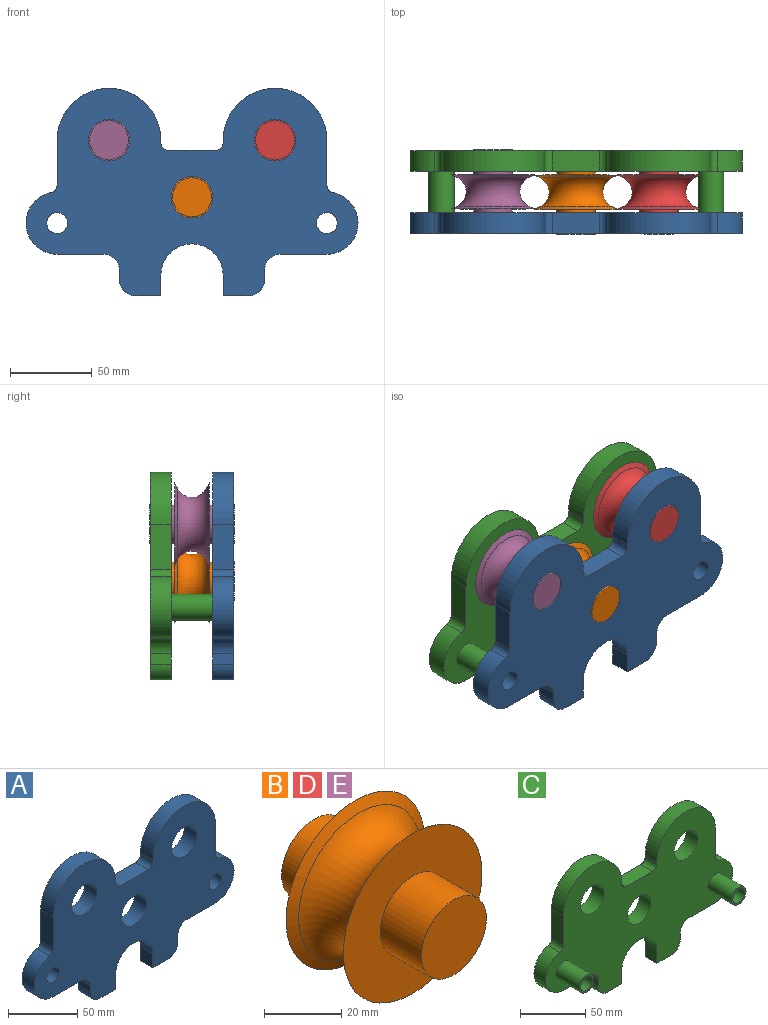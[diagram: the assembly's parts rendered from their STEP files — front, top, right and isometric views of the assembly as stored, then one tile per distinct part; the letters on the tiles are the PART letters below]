
ASSEMBLY  parts=5 mates=4
PART A: 33 faces, bbox 203.2x12.7x127 mm
  f0: plane 15.88x12.7mm, normal (0,0,-1), area 201.6mm2, adj f1,f26,f31,f32
  f1: cylinder r=9.53mm len=12.7mm, axis (0,1,0), area 190mm2, adj f0,f2,f31,f32
  f2: plane 12.7x6.35mm, normal (1,0,0), area 80.6mm2, adj f1,f3,f31,f32
  f3: cylinder r=9.53mm len=12.7mm, axis (0,1,0), area 190mm2, adj f2,f4,f31,f32
  f4: plane 28.58x12.7mm, normal (0,0,-1), area 362.9mm2, adj f3,f5,f31,f32
  f5: cylinder r=19.05mm len=37.72mm, axis (0,1,0), area 711.3mm2, adj f4,f6,f31,f32
  f6: cylinder r=4.76mm len=12.7mm, axis (0,1,0), area 82.8mm2, adj f5,f7,f31,f32
  f7: plane 27.47x12.7mm, normal (1,0,0), area 348.9mm2, adj f6,f8,f31,f32
  f8: cylinder r=31.75mm len=63.5mm, axis (0,1,0), area 1266.8mm2, adj f7,f9,f31,f32
  f9: plane 12.7x1.59mm, normal (-1,0,0), area 20.2mm2, adj f8,f10,f31,f32
  f10: cylinder r=4.76mm len=12.7mm, axis (0,1,0), area 95mm2, adj f9,f11,f31,f32
  f11: plane 28.58x12.7mm, normal (0,0,1), area 362.9mm2, adj f10,f12,f31,f32
  f12: cylinder r=4.76mm len=12.7mm, axis (0,1,0), area 95mm2, adj f11,f13,f31,f32
  f13: plane 12.7x1.59mm, normal (1,0,0), area 20.2mm2, adj f12,f14,f31,f32
  f14: cylinder r=31.75mm len=63.5mm, axis (0,1,0), area 1266.8mm2, adj f13,f15,f31,f32
  f15: plane 27.47x12.7mm, normal (-1,0,0), area 348.9mm2, adj f14,f16,f31,f32
  f16: cylinder r=4.76mm len=12.7mm, axis (0,1,0), area 82.8mm2, adj f15,f17,f31,f32
  f17: cylinder r=19.05mm len=37.72mm, axis (0,1,0), area 711.3mm2, adj f16,f18,f31,f32
  f18: plane 28.58x12.7mm, normal (0,0,-1), area 362.9mm2, adj f17,f19,f31,f32
  f19: cylinder r=9.53mm len=12.7mm, axis (0,1,0), area 190mm2, adj f18,f20,f31,f32
  f20: plane 12.7x6.35mm, normal (-1,0,0), area 80.6mm2, adj f19,f21,f31,f32
  f21: cylinder r=9.53mm len=12.7mm, axis (0,1,0), area 190mm2, adj f20,f22,f31,f32
  f22: plane 15.88x12.7mm, normal (0,0,-1), area 201.6mm2, adj f21,f23,f31,f32
  f23: plane 12.7x12.7mm, normal (1,0,0), area 161.3mm2, adj f22,f24,f31,f32
  f24: cylinder r=19.05mm len=38.1mm, axis (0,1,0), area 760.1mm2, adj f23,f26,f31,f32
  f25: cylinder r=6.35mm len=12.7mm, axis (0,1,0), area 506.7mm2, adj f31,f32
  f26: plane 12.7x12.7mm, normal (-1,0,0), area 161.3mm2, adj f0,f24,f31,f32
  f27: cylinder r=12.7mm len=25.4mm, axis (0,1,0), area 1013.4mm2, adj f31,f32
  f28: cylinder r=12.7mm len=25.4mm, axis (0,1,0), area 1013.4mm2, adj f31,f32
  f29: cylinder r=12.7mm len=25.4mm, axis (0,1,0), area 1013.4mm2, adj f31,f32
  f30: cylinder r=6.35mm len=12.7mm, axis (0,1,0), area 506.7mm2, adj f31,f32
  f31: plane 203.2x127mm, normal (0,-1,0), area 15044.7mm2, adj f0,f1,f2,f3,f4,f5,f6,f7
  f32: plane 203.2x127mm, normal (0,1,0), area 15044.7mm2, adj f0,f1,f2,f3,f4,f5,f6,f7
PART B: 9 faces, bbox 57.2x51.2x57.2 mm
  f0: plane 23.81x23.81mm, normal (0,1,0), area 445.3mm2, adj f1
  f1: cylinder r=11.91mm len=23.81mm, axis (0,-1,0), area 1129.6mm2, adj f0,f2
  f2: plane 50.8x50.8mm, normal (0,1,0), area 1581.5mm2, adj f1,f3
  f3: cone r=25.4mm half-angle=65deg, axis (0,1,0), area 524.1mm2, adj f2,f4
  f4: torus R=26.44mm, axis (0,-1,0), area 2625.5mm2, adj f3,f5
  f5: cone r=25.4mm half-angle=65deg, axis (0,-1,0), area 524.1mm2, adj f4,f6
  f6: plane 50.8x50.8mm, normal (0,-1,0), area 1581.5mm2, adj f5,f7
  f7: cylinder r=11.91mm len=23.81mm, axis (0,-1,0), area 1129.6mm2, adj f6,f8
  f8: plane 23.81x23.81mm, normal (0,-1,0), area 445.3mm2, adj f7
PART C: 37 faces, bbox 203.2x38.1x127 mm
  f0: plane 15.88x12.7mm, normal (0,0,-1), area 201.6mm2, adj f1,f26,f31,f32
  f1: cylinder r=9.53mm len=12.7mm, axis (0,-1,0), area 190mm2, adj f0,f2,f31,f32
  f2: plane 12.7x6.35mm, normal (1,0,0), area 80.6mm2, adj f1,f3,f31,f32
  f3: cylinder r=9.53mm len=12.7mm, axis (0,-1,0), area 190mm2, adj f2,f4,f31,f32
  f4: plane 28.58x12.7mm, normal (0,0,-1), area 362.9mm2, adj f3,f5,f31,f32
  f5: cylinder r=19.05mm len=37.72mm, axis (0,-1,0), area 711.3mm2, adj f4,f6,f31,f32
  f6: cylinder r=4.76mm len=12.7mm, axis (0,-1,0), area 82.8mm2, adj f5,f7,f31,f32
  f7: plane 27.47x12.7mm, normal (1,0,0), area 348.9mm2, adj f6,f8,f31,f32
  f8: cylinder r=31.75mm len=63.5mm, axis (0,-1,0), area 1266.8mm2, adj f7,f9,f31,f32
  f9: plane 12.7x1.59mm, normal (-1,0,0), area 20.2mm2, adj f8,f10,f31,f32
  f10: cylinder r=4.76mm len=12.7mm, axis (0,-1,0), area 95mm2, adj f9,f11,f31,f32
  f11: plane 28.58x12.7mm, normal (0,0,1), area 362.9mm2, adj f10,f12,f31,f32
  f12: cylinder r=4.76mm len=12.7mm, axis (0,-1,0), area 95mm2, adj f11,f13,f31,f32
  f13: plane 12.7x1.59mm, normal (1,0,0), area 20.2mm2, adj f12,f14,f31,f32
  f14: cylinder r=31.75mm len=63.5mm, axis (0,-1,0), area 1266.8mm2, adj f13,f15,f31,f32
  f15: plane 27.47x12.7mm, normal (-1,0,0), area 348.9mm2, adj f14,f16,f31,f32
  f16: cylinder r=4.76mm len=12.7mm, axis (0,-1,0), area 82.8mm2, adj f15,f17,f31,f32
  f17: cylinder r=19.05mm len=37.72mm, axis (0,-1,0), area 711.3mm2, adj f16,f18,f31,f32
  f18: plane 28.58x12.7mm, normal (0,0,-1), area 362.9mm2, adj f17,f19,f31,f32
  f19: cylinder r=9.53mm len=12.7mm, axis (0,-1,0), area 190mm2, adj f18,f20,f31,f32
  f20: plane 12.7x6.35mm, normal (-1,0,0), area 80.6mm2, adj f19,f21,f31,f32
  f21: cylinder r=9.53mm len=12.7mm, axis (0,-1,0), area 190mm2, adj f20,f22,f31,f32
  f22: plane 15.88x12.7mm, normal (0,0,-1), area 201.6mm2, adj f21,f23,f31,f32
  f23: plane 12.7x12.7mm, normal (1,0,0), area 161.3mm2, adj f22,f24,f31,f32
  f24: cylinder r=19.05mm len=38.1mm, axis (0,-1,0), area 760.1mm2, adj f23,f26,f31,f32
  f25: cylinder r=6.35mm len=38.1mm, axis (0,-1,0), area 1520.1mm2, adj f31,f34
  f26: plane 12.7x12.7mm, normal (-1,0,0), area 161.3mm2, adj f0,f24,f31,f32
  f27: cylinder r=12.7mm len=25.4mm, axis (0,-1,0), area 1013.4mm2, adj f31,f32
  f28: cylinder r=12.7mm len=25.4mm, axis (0,-1,0), area 1013.4mm2, adj f31,f32
  f29: cylinder r=12.7mm len=25.4mm, axis (0,-1,0), area 1013.4mm2, adj f31,f32
  f30: cylinder r=6.35mm len=38.1mm, axis (0,-1,0), area 1520.1mm2, adj f31,f36
  f31: plane 203.2x127mm, normal (0,1,0), area 15044.7mm2, adj f0,f1,f2,f3,f4,f5,f6,f7
  f32: plane 203.2x127mm, normal (0,-1,0), area 14902.2mm2, adj f0,f1,f2,f3,f4,f5,f6,f7
  f33: cylinder r=7.94mm len=25.4mm, axis (0,1,0), area 1266.8mm2, adj f32,f34
  f34: plane 15.88x15.88mm, normal (0,-1,0), area 71.3mm2, adj f25,f33
  f35: cylinder r=7.94mm len=25.4mm, axis (0,1,0), area 1266.8mm2, adj f32,f36
  f36: plane 15.88x15.88mm, normal (0,-1,0), area 71.3mm2, adj f30,f35
PART D: same geometry as B
PART E: same geometry as B
PLACE A t=(-39.61,-31.57,85.03)mm
PLACE B t=(-39.61,-12.63,85.03)mm
PLACE C t=(-39.61,0.18,85.03)mm
PLACE D t=(11.19,-12.63,119.95)mm
PLACE E t=(-90.41,-12.42,119.95)mm
MATE cylindrical D.f1 <-> C.f8  axis (0,-1,0) through (11.19,5.43,119.95)mm
MATE fastened C.f17 <-> A.f17  axis (0,-1,0) through (-122.16,-25.22,69.15)mm
MATE cylindrical B.f1 <-> C.f27  axis (0,-1,0) through (-39.61,5.43,85.03)mm
MATE cylindrical E.f1 <-> A.f14  axis (0,-1,0) through (-90.41,-30.48,119.95)mm
